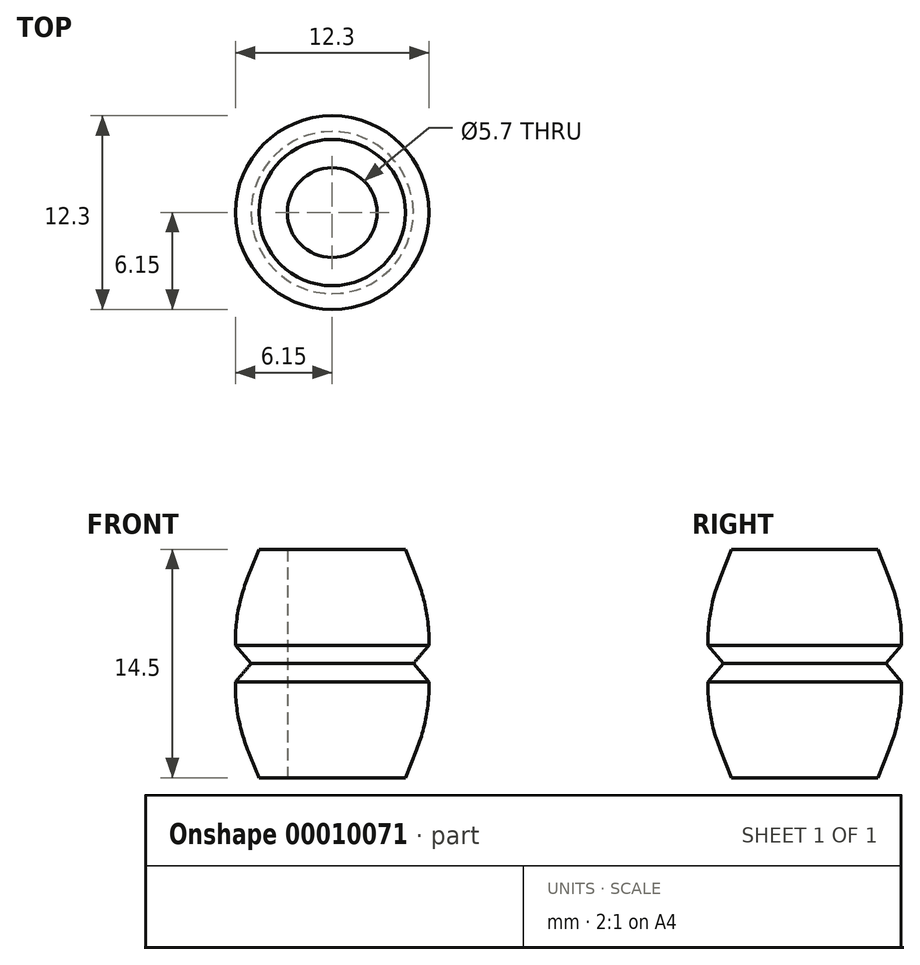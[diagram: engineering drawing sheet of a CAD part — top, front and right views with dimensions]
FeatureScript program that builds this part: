
annotation { "Feature Type Name" : "Feature", "Feature Type Description" : "" }
export const myFeature = defineFeature(function(context is Context, id is Id, definition is map)
    precondition{}
    {
        {
            var Q0;
            Q0=qCreatedBy(makeId("Right.planeOp"),FACE);
            var sketch = newSketch(context, id + "F0", { "sketchPlane" : qUnion([Q0])});
            skLineSegment(sketch, "E0", {"start": v(0, -7.25) * mm, "end": v(0, 7.25) * mm, "construction": true});
            skLineSegment(sketch, "E1", {"start": v(2.85, 7.25) * mm, "end": v(2.85, -7.25) * mm});
            skLineSegment(sketch, "E2", {"start": v(2.85, -7.25) * mm, "end": v(4.65, -7.25) * mm});
            skLineSegment(sketch, "E3", {"start": v(4.65, -7.25) * mm, "end": v(6.65, -2.25) * mm});
            skLineSegment(sketch, "E4", {"start": v(6.65, 2.25) * mm, "end": v(4.65, 7.25) * mm});
            skLineSegment(sketch, "E5", {"start": v(4.65, 7.25) * mm, "end": v(2.85, 7.25) * mm});
            skLineSegment(sketch, "E6", {"start": v(6.65, -2.25) * mm, "end": v(6.65, -1.75) * mm});
            skLineSegment(sketch, "E7", {"start": v(6.65, 2.25) * mm, "end": v(6.65, 1.75) * mm});
            skLineSegment(sketch, "E8", {"start": v(6.65, 1.75) * mm, "end": v(5.15, 0) * mm});
            skLineSegment(sketch, "E9", {"start": v(5.15, 0) * mm, "end": v(6.65, -1.75) * mm});
            skSolve(sketch);
        }
        {
            var Q0;
            Q0=makeQuery(id+"F0.imprint","IMPRINT",FACE,{"disambiguationData":[TD([[makeQuery(id+"F0.imprint","IMPRINT",EDGE,{"derivedFrom":sQuery(id+"F0.wireOp",EDGE,"E1")}),1.0]])]});
            var Q1;
            Q1=sQuery(id+"F0.wireOp",EDGE,"E0");
            revolve(context, id + "F1", {"entities" : qUnion([Q0]), "axis" : qUnion([Q1]), "revolveType" : RevolveType.FULL});
        }
        {
            var Q0;
            Q0=makeQuery(id+"F1.opRevolve","SWEPT_FACE",FACE,{"disambiguationData":[OSD([sQuery(id+"F0.wireOp",EDGE,"E5")])]});
            var sketch = newSketch(context, id + "F2", { "sketchPlane" : qUnion([Q0])});
            skCircle(sketch, "E10", {"center": v(0, 0) * mm, "radius": 7.5 * mm});
            skCircle(sketch, "E11", {"center": v(0, 0) * mm, "radius": 6.15 * mm});
            skSolve(sketch);
        }
        {
            var Q0;
            Q0=makeQuery(id+"F2.imprint","IMPRINT",FACE,{"disambiguationData":[TD([[makeQuery(id+"F2.imprint","IMPRINT",EDGE,{"derivedFrom":sQuery(id+"F2.wireOp",EDGE,"E10")}),1.0]])]});
            extrude(context, id + "F3", {"entities" : qUnion([Q0]), "operationType" : NewBodyOperationType.REMOVE, "oppositeDirection" : true, "depth" : 25 * mm});
        }
        {
            var Q0;
            Q0=makeQuery(id+"F3.boolean.opBoolean","INTERSECT",EDGE,{"derivedFrom":[makeQuery(id+"F1.opRevolve","SWEPT_FACE",FACE,{"disambiguationData":[OSD([sQuery(id+"F0.wireOp",EDGE,"E4")])]}),makeQuery(id+"F3.opExtrude","SWEPT_FACE",FACE,{"disambiguationData":[OSD([sQuery(id+"F2.wireOp",EDGE,"E11")])]})]});
            var Q1;
            Q1=makeQuery(id+"F3.boolean.opBoolean","INTERSECT",EDGE,{"derivedFrom":[makeQuery(id+"F1.opRevolve","SWEPT_FACE",FACE,{"disambiguationData":[OSD([sQuery(id+"F0.wireOp",EDGE,"E3")])]}),makeQuery(id+"F3.opExtrude","SWEPT_FACE",FACE,{"disambiguationData":[OSD([sQuery(id+"F2.wireOp",EDGE,"E11")])]})]});
            fillet(context, id + "F4", {"entities" : qUnion([Q0, Q1]), "radius" : 11 * mm, "tangentPropagation" : true, "allowEdgeOverflow" : false});
        }
    });
